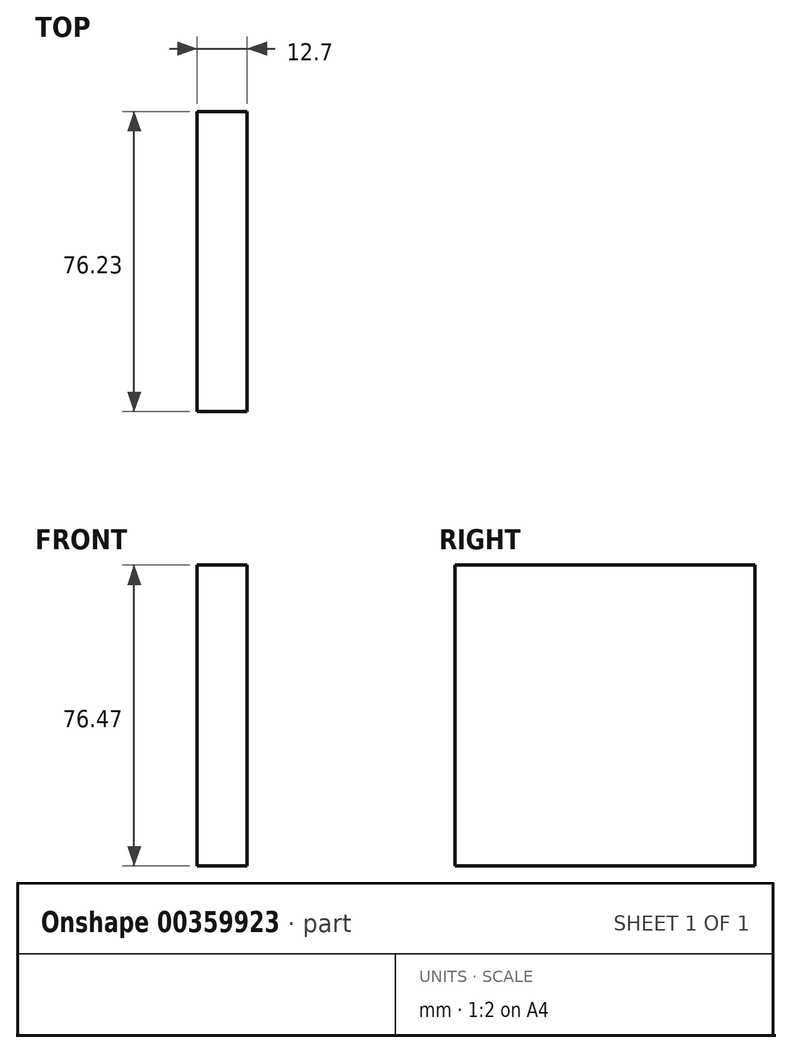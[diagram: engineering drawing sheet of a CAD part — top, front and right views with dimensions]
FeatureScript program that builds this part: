
annotation { "Feature Type Name" : "Feature", "Feature Type Description" : "" }
export const myFeature = defineFeature(function(context is Context, id is Id, definition is map)
    precondition{}
    {
        {
            var Q0;
            Q0=qCreatedBy(makeId("Front.planeOp"),FACE);
            var sketch = newSketch(context, id + "F0", { "sketchPlane" : qUnion([Q0])});
            skLineSegment(sketch, "E0.bottom", {"start": v(0, 0) * mm, "end": v(12.7, 0) * mm});
            skLineSegment(sketch, "E0.top", {"start": v(0, -63.5) * mm, "end": v(12.7, -63.5) * mm});
            skLineSegment(sketch, "E0.left", {"start": v(0, 0) * mm, "end": v(0, -63.5) * mm});
            skLineSegment(sketch, "E0.right", {"start": v(12.7, 0) * mm, "end": v(12.7, -63.5) * mm});
            skSolve(sketch);
        }
        {
            var Q0;
            Q0 = qSketchRegion(id + "F0", true);
            extrude(context, id + "F1", {"entities" : qUnion([Q0]), "depth" : 76.23 * mm});
        }
        {
            var Q0;
            Q0=makeQuery(id+"F1.opExtrude","SWEPT_FACE",FACE,{"disambiguationData":[OSD([sQuery(id+"F0.wireOp",EDGE,"E0.top")])]});
            extrude(context, id + "F2", {"entities" : qUnion([Q0]), "operationType" : NewBodyOperationType.ADD, "depth" : 12.97 * mm});
        }
    });
